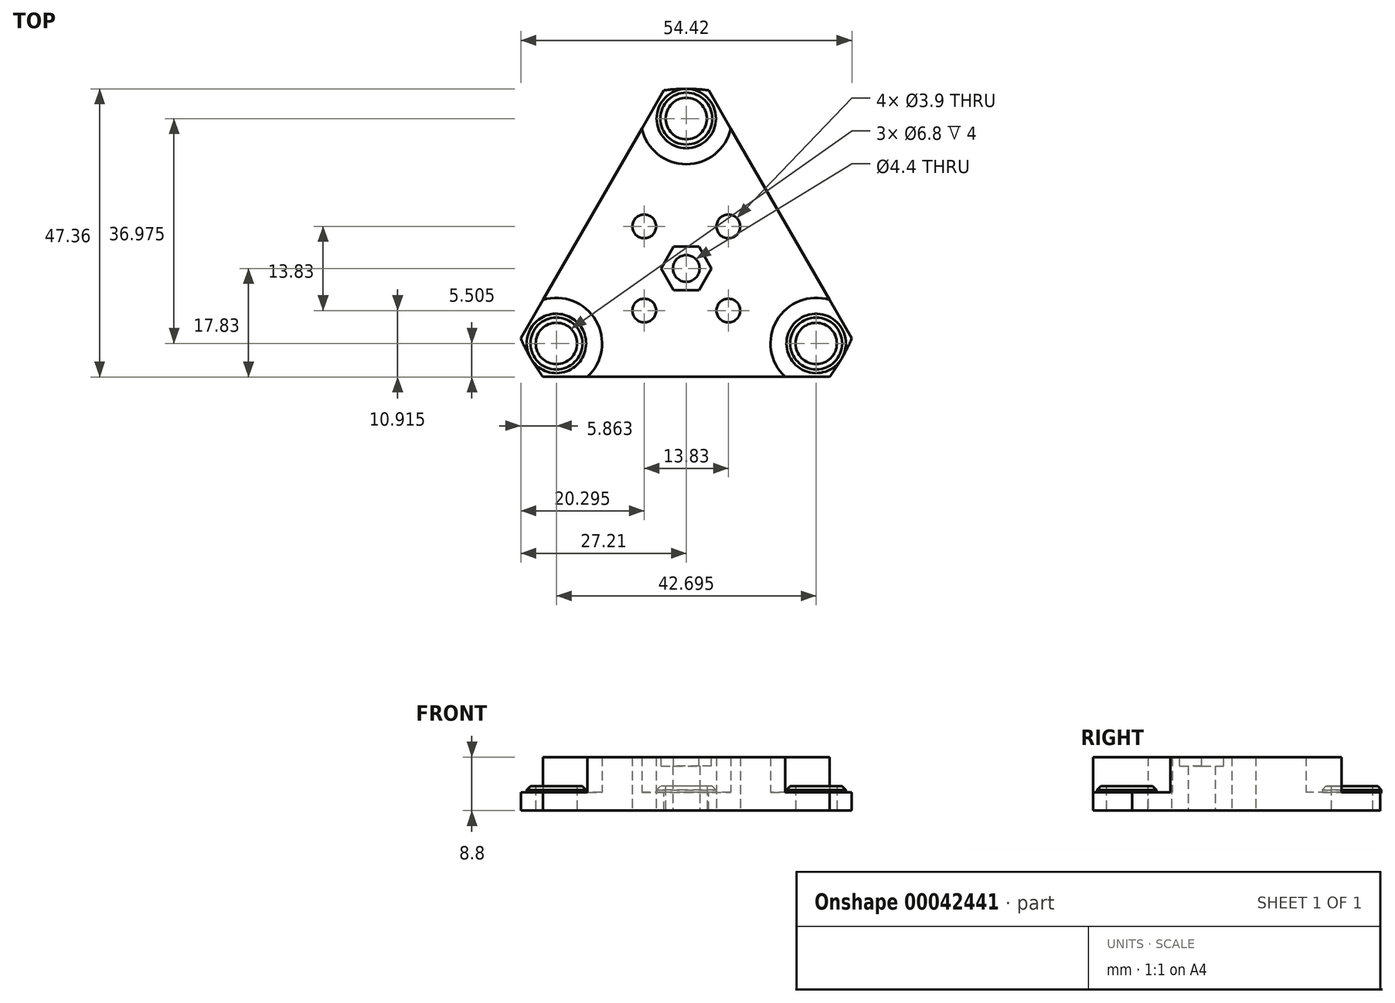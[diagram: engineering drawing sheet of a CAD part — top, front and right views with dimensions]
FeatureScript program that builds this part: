
annotation { "Feature Type Name" : "Feature", "Feature Type Description" : "" }
export const myFeature = defineFeature(function(context is Context, id is Id, definition is map)
    precondition{}
    {
        {
            var Q0;
            Q0=qCreatedBy(makeId("Top.planeOp"),FACE);
            var sketch = newSketch(context, id + "F0", { "sketchPlane" : qUnion([Q0])});
            skCircle(sketch, "E0", {"center": v(0, 0) * mm, "radius": 30 * mm, "construction": true});
            skCircle(sketch, "E1", {"center": v(0, 0) * mm, "radius": 31 * mm, "construction": true});
            skLineSegment(sketch, "E2", {"start": v(0, 30) * mm, "end": v(0, 31) * mm, "construction": true});
            skLineSegment(sketch, "E3", {"start": v(0, 30) * mm, "end": v(0, 0) * mm, "construction": true});
            skCircle(sketch, "E4", {"center": v(0, 24.65) * mm, "radius": 6.35 * mm, "construction": true});
            skCircle(sketch, "E5", {"center": v(0, 24.65) * mm, "radius": 3.4 * mm});
            skCircle(sketch, "E6.1.0", {"center": v(-21.35, -12.32) * mm, "radius": 3.4 * mm});
            skCircle(sketch, "E6.2.0", {"center": v(21.35, -12.33) * mm, "radius": 3.4 * mm});
            skLineSegment(sketch, "E7", {"start": v(-24.3, -14.02) * mm, "end": v(-26.85, -15.5) * mm, "construction": true});
            skPoint(sketch, "E8", {"position": v(-25.57, -14.76) * mm});
            skCircle(sketch, "E9", {"center": v(0, 0) * mm, "radius": 29.52 * mm});
            skSolve(sketch);
        }
        {
            var Q0;
            Q0=qSketchRegion(id+"F0",true);
            extrude(context, id + "F1", {"entities" : qUnion([Q0]), "depth" : 3 * mm});
        }
        {
            var Q0;
            Q0=makeQuery(id+"F1.opExtrude","CAP_FACE",FACE,{"disambiguationData":[OSD([sQuery(id+"F0.wireOp",EDGE,"E5"),sQuery(id+"F0.wireOp",EDGE,"E6.1.0"),sQuery(id+"F0.wireOp",EDGE,"E6.2.0"),sQuery(id+"F0.wireOp",EDGE,"E9")])],"isStart":false});
            var sketch = newSketch(context, id + "F2", { "sketchPlane" : qUnion([Q0])});
            skCircle(sketch, "E10", {"center": v(0, 24.65) * mm, "radius": 4.88 * mm});
            skCircle(sketch, "E11", {"center": v(21.35, -12.33) * mm, "radius": 4.88 * mm});
            skCircle(sketch, "E12", {"center": v(-21.35, -12.32) * mm, "radius": 4.87 * mm});
            skCircle(sketch, "E13.0", {"center": v(0, 24.65) * mm, "radius": 3.4 * mm});
            skCircle(sketch, "E13.1", {"center": v(-21.35, -12.32) * mm, "radius": 3.4 * mm});
            skCircle(sketch, "E13.2", {"center": v(21.35, -12.33) * mm, "radius": 3.4 * mm});
            skSolve(sketch);
        }
        {
            var Q0;
            Q0=qSketchRegion(id+"F2",true);
            extrude(context, id + "F3", {"entities" : qUnion([Q0]), "operationType" : NewBodyOperationType.ADD, "depth" : 1 * mm});
        }
        {
            var Q0;
            Q0=makeQuery(id+"F3.opExtrude","CAP_EDGE",EDGE,{"disambiguationData":[OSD([sQuery(id+"F2.wireOp",EDGE,"E12")])],"isStart":false});
            var Q1;
            Q1=makeQuery(id+"F3.opExtrude","CAP_EDGE",EDGE,{"disambiguationData":[OSD([sQuery(id+"F2.wireOp",EDGE,"E11")])],"isStart":false});
            var Q2;
            Q2=makeQuery(id+"F3.opExtrude","CAP_EDGE",EDGE,{"disambiguationData":[OSD([sQuery(id+"F2.wireOp",EDGE,"E10")])],"isStart":false});
            chamfer(context, id + "F4", {"entities" : qUnion([Q0, Q1, Q2]), "width" : 0.6 * mm, "tangentPropagation" : true});
        }
        {
            var Q0;
            Q0=makeQuery(id+"F1.opExtrude","CAP_FACE",FACE,{"disambiguationData":[OSD([sQuery(id+"F0.wireOp",EDGE,"E5"),sQuery(id+"F0.wireOp",EDGE,"E6.1.0"),sQuery(id+"F0.wireOp",EDGE,"E6.2.0"),sQuery(id+"F0.wireOp",EDGE,"E9")])],"isStart":false});
            var sketch = newSketch(context, id + "F5", { "sketchPlane" : qUnion([Q0])});
            skCircle(sketch, "E14", {"center": v(0, 24.65) * mm, "radius": 7.5 * mm, "construction": true});
            skCircle(sketch, "E15", {"center": v(-21.35, -12.32) * mm, "radius": 7.5 * mm, "construction": true});
            skCircle(sketch, "E16", {"center": v(21.35, -12.33) * mm, "radius": 7.5 * mm, "construction": true});
            skLineSegment(sketch, "E17", {"start": v(-6.5, 28.4) * mm, "end": v(-27.84, -8.58) * mm, "construction": true});
            skLineSegment(sketch, "E18", {"start": v(6.5, 28.4) * mm, "end": v(27.84, -8.58) * mm, "construction": true});
            skLineSegment(sketch, "E19", {"start": v(-21.35, -19.82) * mm, "end": v(21.35, -19.82) * mm, "construction": true});
            skLineSegment(sketch, "E20", {"start": v(-7.31, 22.98) * mm, "end": v(-23.56, -5.16) * mm});
            skLineSegment(sketch, "E21", {"start": v(7.31, 22.98) * mm, "end": v(23.56, -5.16) * mm});
            skLineSegment(sketch, "E22", {"start": v(16.25, -17.82) * mm, "end": v(-16.25, -17.82) * mm});
            skLineSegment(sketch, "E23", {"start": v(0, -17.82) * mm, "end": v(0, -19.82) * mm, "construction": true});
            skLineSegment(sketch, "E24", {"start": v(-15.44, 8.91) * mm, "end": v(-17.17, 9.91) * mm, "construction": true});
            skLineSegment(sketch, "E25", {"start": v(15.44, 8.91) * mm, "end": v(17.17, 9.91) * mm, "construction": true});
            skArc(sketch, "E26", {"start": v(-7.31, 22.98) * mm, "mid": v(0, 17.15) * mm, "end": v(7.31, 22.98) * mm});
            skArc(sketch, "E27", {"start": v(23.56, -5.16) * mm, "mid": v(14.85, -8.57) * mm, "end": v(16.25, -17.82) * mm});
            skArc(sketch, "E28", {"start": v(-16.25, -17.82) * mm, "mid": v(-14.85, -8.58) * mm, "end": v(-23.56, -5.16) * mm});
            skSolve(sketch);
        }
        {
            var Q0;
            Q0=qSketchRegion(id+"F5",true);
            extrude(context, id + "F6", {"entities" : qUnion([Q0]), "operationType" : NewBodyOperationType.ADD, "depth" : 5.8 * mm});
        }
        {
            var Q0;
            Q0=makeQuery(id+"F1.opExtrude","CAP_FACE",FACE,{"disambiguationData":[OSD([sQuery(id+"F0.wireOp",EDGE,"E5"),sQuery(id+"F0.wireOp",EDGE,"E6.1.0"),sQuery(id+"F0.wireOp",EDGE,"E6.2.0"),sQuery(id+"F0.wireOp",EDGE,"E9")])],"isStart":true});
            var sketch = newSketch(context, id + "F7", { "sketchPlane" : qUnion([Q0])});
            skLineSegment(sketch, "E29", {"start": v(0, 0) * mm, "end": v(0, -24.65) * mm, "construction": true});
            skCircle(sketch, "E30.cCircle", {"center": v(0, 0) * mm, "radius": 9.78 * mm, "construction": true});
            skLineSegment(sketch, "E30.0", {"start": v(6.91, -6.91) * mm, "end": v(-6.91, -6.91) * mm, "construction": true});
            skLineSegment(sketch, "E30.1", {"start": v(-6.91, -6.91) * mm, "end": v(-6.91, 6.91) * mm, "construction": true});
            skLineSegment(sketch, "E30.2", {"start": v(-6.91, 6.91) * mm, "end": v(6.91, 6.91) * mm, "construction": true});
            skLineSegment(sketch, "E30.3", {"start": v(6.91, 6.91) * mm, "end": v(6.91, -6.91) * mm, "construction": true});
            skCircle(sketch, "E31", {"center": v(6.91, 6.91) * mm, "radius": 1.95 * mm});
            skCircle(sketch, "E32.1.0", {"center": v(-6.91, 6.91) * mm, "radius": 1.95 * mm});
            skCircle(sketch, "E32.2.0", {"center": v(-6.91, -6.91) * mm, "radius": 1.95 * mm});
            skCircle(sketch, "E32.3.0", {"center": v(6.91, -6.91) * mm, "radius": 1.95 * mm});
            skSolve(sketch);
        }
        {
            var Q0;
            Q0=qSketchRegion(id+"F7",true);
            extrude(context, id + "F8", {"entities" : qUnion([Q0]), "operationType" : NewBodyOperationType.REMOVE, "endBound" : BoundingType.THROUGH_ALL, "oppositeDirection" : true, "depth" : 25 * mm});
        }
        {
            var Q0;
            Q0=makeQuery(id+"F6.opExtrude","CAP_FACE",FACE,{"disambiguationData":[OSD([sQuery(id+"F5.wireOp",EDGE,"E20"),sQuery(id+"F5.wireOp",EDGE,"E21"),sQuery(id+"F5.wireOp",EDGE,"E22"),sQuery(id+"F5.wireOp",EDGE,"b30b8c31-8519-46e4-bd01-4f495bb6e8cf"),sQuery(id+"F5.wireOp",EDGE,"E26"),sQuery(id+"F5.wireOp",EDGE,"E27")])],"isStart":false});
            var sketch = newSketch(context, id + "F9", { "sketchPlane" : qUnion([Q0])});
            skCircle(sketch, "E33.cCircle", {"center": v(0, 0) * mm, "radius": 3.6 * mm, "construction": true});
            skLineSegment(sketch, "E33.0", {"start": v(-2.08, 3.6) * mm, "end": v(2.08, 3.6) * mm});
            skLineSegment(sketch, "E33.1", {"start": v(2.08, 3.6) * mm, "end": v(4.16, 0) * mm});
            skLineSegment(sketch, "E33.2", {"start": v(4.16, 0) * mm, "end": v(2.08, -3.6) * mm});
            skLineSegment(sketch, "E33.3", {"start": v(2.08, -3.6) * mm, "end": v(-2.08, -3.6) * mm});
            skLineSegment(sketch, "E33.4", {"start": v(-2.08, -3.6) * mm, "end": v(-4.16, 0) * mm});
            skLineSegment(sketch, "E33.5", {"start": v(-4.16, 0) * mm, "end": v(-2.08, 3.6) * mm});
            skPoint(sketch, "E33.0.midPoint", {"position": v(0, 3.6) * mm});
            skSolve(sketch);
        }
        {
            var Q0;
            Q0=qSketchRegion(id+"F9",true);
            extrude(context, id + "F10", {"entities" : qUnion([Q0]), "operationType" : NewBodyOperationType.REMOVE, "oppositeDirection" : true, "depth" : 1.45 * mm});
        }
        {
            var Q0;
            Q0=makeQuery(id+"F1.opExtrude","CAP_FACE",FACE,{"disambiguationData":[OSD([sQuery(id+"F0.wireOp",EDGE,"E5"),sQuery(id+"F0.wireOp",EDGE,"E6.1.0"),sQuery(id+"F0.wireOp",EDGE,"E6.2.0"),sQuery(id+"F0.wireOp",EDGE,"E9")])],"isStart":true});
            var sketch = newSketch(context, id + "F11", { "sketchPlane" : qUnion([Q0])});
            skCircle(sketch, "E34", {"center": v(0, 0) * mm, "radius": 2.2 * mm});
            skSolve(sketch);
        }
        {
            var Q0;
            Q0=qSketchRegion(id+"F11",true);
            extrude(context, id + "F12", {"entities" : qUnion([Q0]), "operationType" : NewBodyOperationType.REMOVE, "endBound" : BoundingType.THROUGH_ALL, "oppositeDirection" : true, "depth" : 25 * mm});
        }
        {
            var Q0;
            Q0=makeQuery(id+"F1.opExtrude","CAP_FACE",FACE,{"disambiguationData":[OSD([sQuery(id+"F0.wireOp",EDGE,"E5"),sQuery(id+"F0.wireOp",EDGE,"E6.1.0"),sQuery(id+"F0.wireOp",EDGE,"E6.2.0"),sQuery(id+"F0.wireOp",EDGE,"E9")])],"isStart":false});
            var sketch = newSketch(context, id + "F13", { "sketchPlane" : qUnion([Q0])});
            skLineSegment(sketch, "E35", {"start": v(27.2, -11.47) * mm, "end": v(3.67, 29.3) * mm});
            skLineSegment(sketch, "E36.1.0", {"start": v(-3.67, 29.3) * mm, "end": v(-27.2, -11.47) * mm});
            skLineSegment(sketch, "E36.2.0", {"start": v(-23.54, -17.82) * mm, "end": v(23.54, -17.82) * mm});
            skPoint(sketch, "E36.center", {"position": v(0, 0) * mm});
            skArc(sketch, "E37.0", {"start": v(-3.67, 29.3) * mm, "mid": v(-25.57, 14.76) * mm, "end": v(-27.2, -11.47) * mm});
            skArc(sketch, "E38.0", {"start": v(27.2, -11.47) * mm, "mid": v(25.57, 14.76) * mm, "end": v(3.67, 29.3) * mm});
            skArc(sketch, "E39.0", {"start": v(-23.54, -17.82) * mm, "mid": v(0, -29.53) * mm, "end": v(23.54, -17.82) * mm});
            skPoint(sketch, "E40.orphan", {"position": v(-25.57, -14.76) * mm});
            skPoint(sketch, "E41.orphan", {"position": v(0, 29.52) * mm});
            skPoint(sketch, "E42.orphan", {"position": v(25.57, -14.76) * mm});
            skSolve(sketch);
        }
        {
            var Q0;
            Q0=qSketchRegion(id+"F13",true);
            extrude(context, id + "F14", {"entities" : qUnion([Q0]), "operationType" : NewBodyOperationType.REMOVE, "endBound" : BoundingType.THROUGH_ALL, "oppositeDirection" : true, "depth" : 25 * mm});
        }
    });
